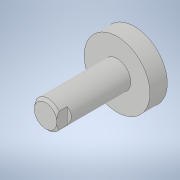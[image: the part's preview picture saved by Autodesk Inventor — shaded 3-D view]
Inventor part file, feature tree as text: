
AUTODESK INVENTOR PART (.ipt)
format: ipt  version: 2020 (Build 240168000, 168)  size: 108,544 bytes
history: native  units: in
note: dims shown in document units (in); Inventor stores cm internally (conversion verified against a paired STEP export)
features: extrude x1, sketch x1, other x1
ambient origin geometry x8: Origin, YZ Plane, XZ Plane, XY Plane, X Axis, Y Axis, Z Axis, Center Point
bodies: Solid1 (feature_tree)
feature tree (3):
  extrude  "Extrusion1"  [1 undecoded]
  sketch  "Sketch1"  dims[d0=0.3937in d1=0.0in]
  other  "External Rod Thread Chamfer"
note: 1 required parameter value undecoded (feature->parameter linkage not recoverable at this tier; creation-order binding heuristic only, values carry confidence <= 0.55)
